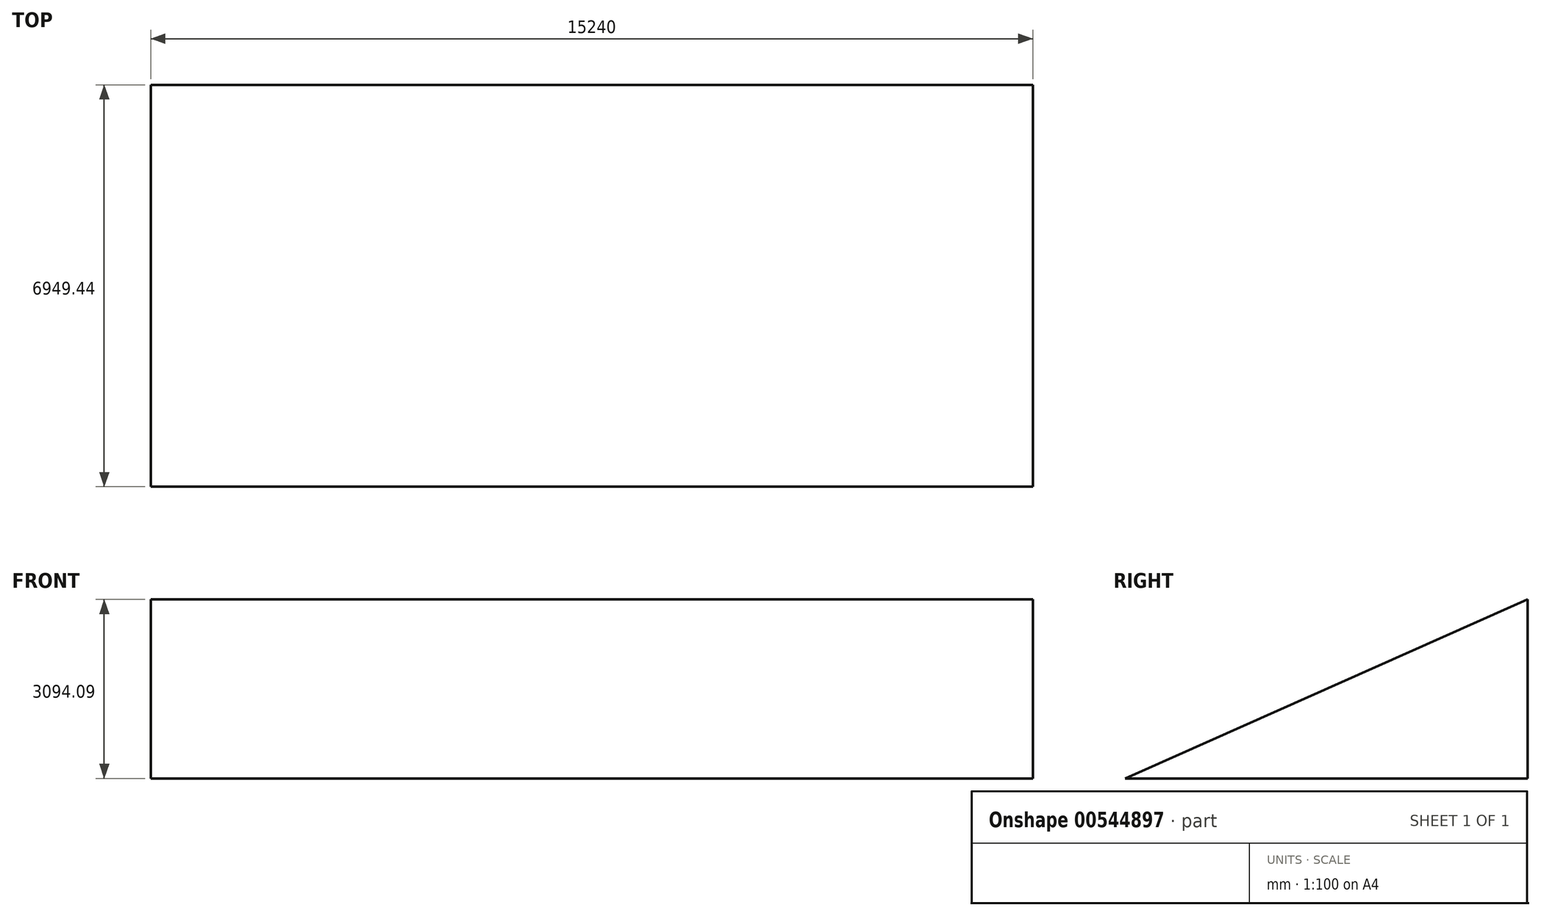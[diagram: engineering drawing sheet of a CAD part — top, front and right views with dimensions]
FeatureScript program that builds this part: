
annotation { "Feature Type Name" : "Feature", "Feature Type Description" : "" }
export const myFeature = defineFeature(function(context is Context, id is Id, definition is map)
    precondition{}
    {
        {
            var Q0;
            Q0=qCreatedBy(makeId("Right.planeOp"),FACE);
            var sketch = newSketch(context, id + "F0", { "sketchPlane" : qUnion([Q0])});
            skLineSegment(sketch, "E0", {"start": v(0, 0) * mm, "end": v(-6949.44, 0) * mm});
            skLineSegment(sketch, "E1", {"start": v(0, 0) * mm, "end": v(0, 3094.1) * mm});
            skLineSegment(sketch, "E2", {"start": v(0, 3094.1) * mm, "end": v(-6949.44, 0) * mm});
            skSolve(sketch);
        }
        {
            var Q0;
            Q0 = qSketchRegion(id + "F0", true);
            extrude(context, id + "F1", {"entities" : qUnion([Q0]), "depth" : 15240 * mm, "offsetDistance" : 25.4 * mm});
        }
    });
